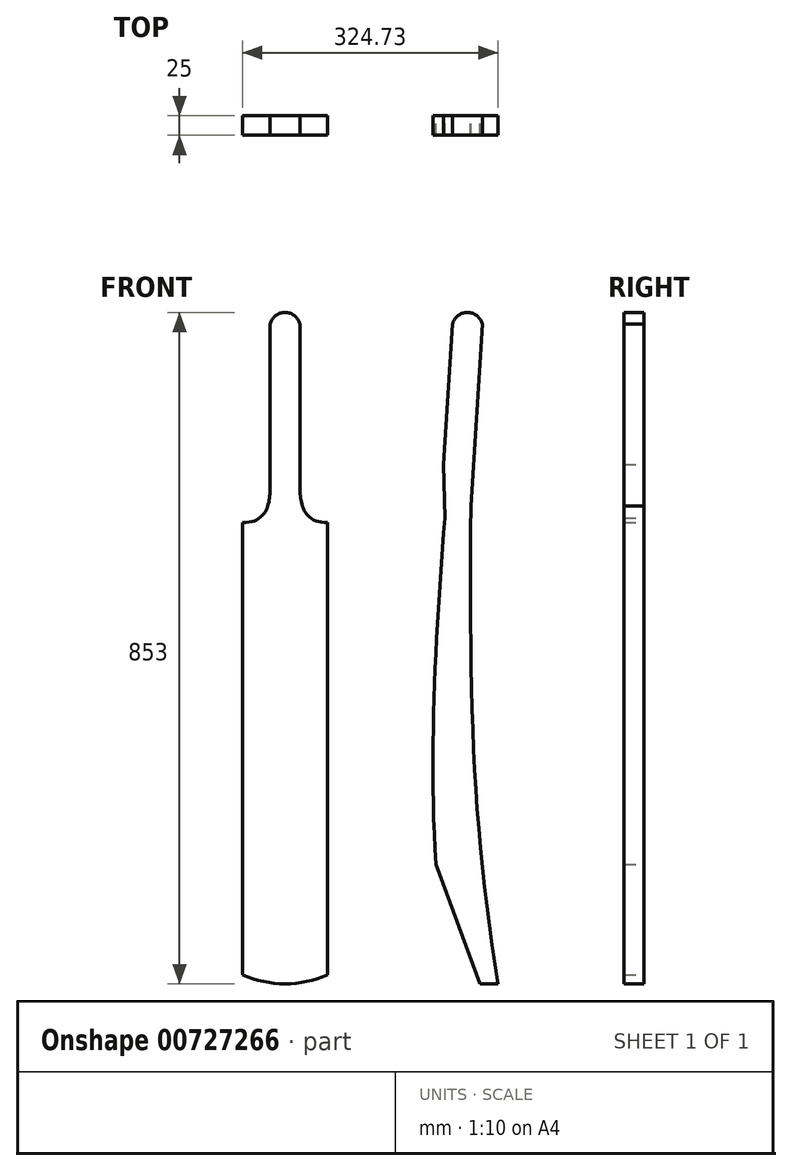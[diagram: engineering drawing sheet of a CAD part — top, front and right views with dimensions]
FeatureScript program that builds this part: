
annotation { "Feature Type Name" : "Feature", "Feature Type Description" : "" }
export const myFeature = defineFeature(function(context is Context, id is Id, definition is map)
    precondition{}
    {
        {
            var Q0;
            Q0=qCreatedBy(makeId("Front.planeOp"),FACE);
            var sketch = newSketch(context, id + "F0", { "sketchPlane" : qUnion([Q0])});
            skLineSegment(sketch, "E0", {"start": v(-56.76, 11.56) * mm, "end": v(-56.76, 585.84) * mm});
            skFitSpline(sketch, "E1", {"points": [v(-56.76, 585.84) * mm, v(-21.76, 632.08) * mm], "startDerivative": vector(102.4, -0.35) * mm, "endDerivative": vector(0, 49.3) * mm});
            skLineSegment(sketch, "E2", {"start": v(-21.76, 632.08) * mm, "end": v(-21.76, 838.13) * mm});
            skLineSegment(sketch, "E3", {"start": v(-2.76, 0) * mm, "end": v(-2.76, 511.29) * mm, "construction": true});
            skFitSpline(sketch, "E4.MirrorCS", {"points": [v(51.24, 585.84) * mm, v(16.24, 632.08) * mm], "startDerivative": vector(-102.4, -0.35) * mm, "endDerivative": vector(0, 49.3) * mm});
            skLineSegment(sketch, "E5.MirrorCS", {"start": v(16.24, 632.08) * mm, "end": v(16.24, 838.13) * mm});
            skLineSegment(sketch, "E6.MirrorCS", {"start": v(51.24, 11.56) * mm, "end": v(51.24, 585.84) * mm});
            skArc(sketch, "E7", {"start": v(-56.76, 11.56) * mm, "mid": v(-2.76, 0) * mm, "end": v(51.24, 11.56) * mm});
            skLineSegment(sketch, "E8", {"start": v(267.97, 0) * mm, "end": v(244.67, 0) * mm});
            skLineSegment(sketch, "E9", {"start": v(244.67, 0) * mm, "end": v(188.99, 152.03) * mm});
            skFitSpline(sketch, "E10", {"points": [v(188.99, 152.03) * mm, v(200.13, 592.07) * mm], "startDerivative": vector(-29.45, 445.6) * mm, "endDerivative": vector(32.57, 442.62) * mm});
            skFitSpline(sketch, "E11", {"points": [v(267.97, 0) * mm, v(233.35, 607.1) * mm], "startDerivative": vector(-97.29, 575.27) * mm, "endDerivative": vector(8.37, 724.35) * mm});
            skLineSegment(sketch, "E12", {"start": v(233.35, 607.1) * mm, "end": v(247.85, 838.13) * mm});
            skArc(sketch, "E13", {"start": v(247.85, 838.13) * mm, "mid": v(228.81, 853) * mm, "end": v(209.78, 838.13) * mm});
            skArc(sketch, "E14", {"start": v(16.24, 838.13) * mm, "mid": v(-2.76, 853) * mm, "end": v(-21.76, 838.13) * mm});
            skLineSegment(sketch, "E15", {"start": v(-175.44, 853) * mm, "end": v(609.6, 853) * mm, "construction": true});
            skLineSegment(sketch, "E16", {"start": v(200.13, 592.07) * mm, "end": v(198.6, 660.08) * mm});
            skLineSegment(sketch, "E17", {"start": v(198.6, 660.08) * mm, "end": v(209.78, 838.13) * mm});
            skPoint(sketch, "E18", {"position": v(246.68, 159.49) * mm});
            skSolve(sketch);
        }
        {
            var Q0;
            Q0 = qSketchRegion(id + "F0", true);
            extrude(context, id + "F1", {"entities" : qUnion([Q0]), "depth" : 25 * mm, "offsetDistance" : 25 * mm});
        }
    });
